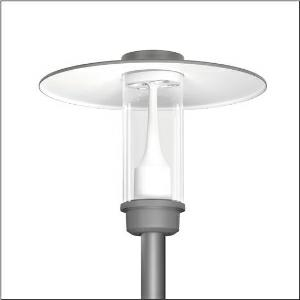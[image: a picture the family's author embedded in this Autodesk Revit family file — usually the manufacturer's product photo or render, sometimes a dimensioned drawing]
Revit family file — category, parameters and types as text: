
# Revit family: litepole_2_iq___p1_0a_5xa5425ff14hp_8674
name_source: partatom
category: Lighting Fixtures
units: mm (PartAtom-declared; Revit-internal decimal feet)

## family parameters
Cut with Voids When Loaded = No
Host = Face
Light Source = No
Part Type = Normal
Room Calculation Point = No
Round Connector Dimension = Use Diameter
Shared = No

## types (1)
- --- (1 x LED, 4730 lm, 33.6 W, 3000K)
    Apparent Load = 34 VA
    CIE Flux Codes = 32 62 90 96 100
    Color Rendering = 70
    Color Temperature = 3000K
    Default Elevation = 1800 mm
    Description = Litepole 2 iQ, mast luminaire, Module 540 iQ-SR, primary light control with 3 zone facetted reflector, of plastic, silver coated, highly specular, structured, primary optical cover: cover, of PMMA, transparent, light distribution: P1.0a, light emission: direct distribution, primary light characteristic: strongly asymmetric, installation type: post-top, LED, High Power LED, rated luminous flux: 4.730lm, luminous efficacy: 141lm/W, light colour: 730, colour temperature: 3000K, control gear: iQ Street-Remote, control: pre-setting: logarithmic dimming characteristic, Street-Remote, Auto-Match, Temp-Guard, Lumen-Switch, Night-Set, Smart-Wire, Light-Fading, Desk-Remote (wireless, voltage-free reading and setting of iQ features in the workshop via application-optimized NFC function/RFID function), optimised constant luminous flux control (CLO 2.0), with terminal, 6-pole, max. 2.5mm², mains connection: 230..240V, AC, 50/60Hz, start of lifetime: 34W, end of service life: 36W, reduction: 15W, luminaire housing, upper part, of aluminium, coated, Siteco® metallic grey (DB 702S), diameter: 750mm, height: 590mm, spigot size: d x l = 76 x 70mm (post-top) | with reducer (optional accessory) 60 x 70mm, mounting height: 3..5m, post-top mast mounting element, of diecast aluminium, coated, Siteco® metallic grey (DB 702S), Module 540 iQ-SR, traffic white (RAL 9016), equipment: Power, protection rating (complete): IP65, insulation class (complete): insulation class II (safety insulation), certification: CE, ENEC, VDE, packaging unit: 1 piece

Light Distribution: P1.0a
    Height = 590 mm
    Lamp = 1 x LED
    Lamp Light Flux = 4730 lm
    Lamp Power = 33.6 W
    Lamp count = 1
    Length = 750 mm
    Luminous efficacy = 141 lm/W
    Manufacturer = Siteco
    ModVariant = No
    Model = 5XA5425FF14HP
    Number of Poles = 1
    OnlyDefault = Yes
    Power Factor = 1
    Product Name = Litepole 2 iQ | P1.0a
    Product group = mast luminaire | pylon top
    ProductGroupID = 6100
    Protection Class = Protection class II
    Protection Degree = IP 65
    RLX_Detail_Level = 1
    RLX_Emergency_Light_Flux = 0 lm
    RLX_Emergency_Type = 0
    RLX_Emergency_Type_DB = No
    RlxData = <blob elided: 32109 chars, md5=df454b07>
    Socket = socket
    Standby Power = 0 W
    System Light Flux = 4730 lm
    System Power = 34 W
    Type Comments = factory setting: luminous flux: 100 % | dim-lin: 254 | 695 mA
    Type Image = l_1006518.jpg
    URL = http://relux.com
    VarID = @adj_189837
    Voltage = 0 V
    Weight = 0.00 kg
    Width = 0 mm  [stored 0 ft]

note: [stored X ft] marks values corroborated as IEEE doubles in the binary element streams (Revit-internal decimal feet)

## geometry (parser evidence)
native form markers: Blend x4, Sweep x8
no freeform markers — native parametric forms only
